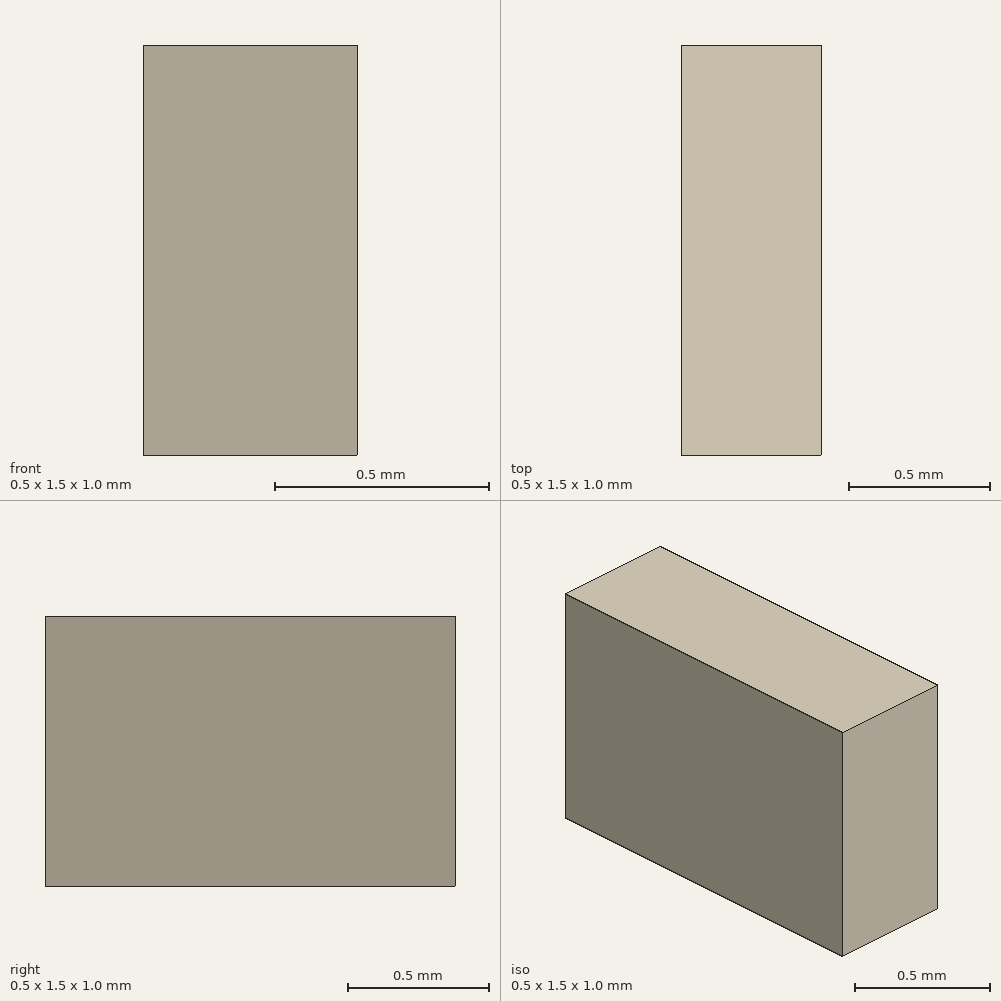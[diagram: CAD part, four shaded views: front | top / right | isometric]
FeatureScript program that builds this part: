
annotation { "Feature Type Name" : "Feature", "Feature Type Description" : "" }
export const myFeature = defineFeature(function(context is Context, id is Id, definition is map)
    precondition{}
    {
        {
            var Q0;
            Q0=qCreatedBy(makeId("Top.planeOp"),FACE);
            var sketch = newSketch(context, id + "F0", { "sketchPlane" : qUnion([Q0])});
            skLineSegment(sketch, "E0.bottom", {"start": v(0, 0) * mm, "end": v(0.5, 0) * mm});
            skLineSegment(sketch, "E0.top", {"start": v(0, -1.46) * mm, "end": v(0.5, -1.46) * mm});
            skLineSegment(sketch, "E0.left", {"start": v(0, 0) * mm, "end": v(0, -1.46) * mm});
            skLineSegment(sketch, "E0.right", {"start": v(0.5, 0) * mm, "end": v(0.5, -1.46) * mm});
            skSolve(sketch);
        }
        {
            var Q0;
            Q0=makeQuery(id+"F0.imprint","IMPRINT",FACE,{"disambiguationData":[TD([[makeQuery(id+"F0.imprint","IMPRINT",EDGE,{"derivedFrom":sQuery(id+"F0.wireOp",EDGE,"E0.bottom")}),-1.0]])]});
            extrude(context, id + "F1", {"entities" : qUnion([Q0]), "depth" : 0.96 * mm});
        }
    });
